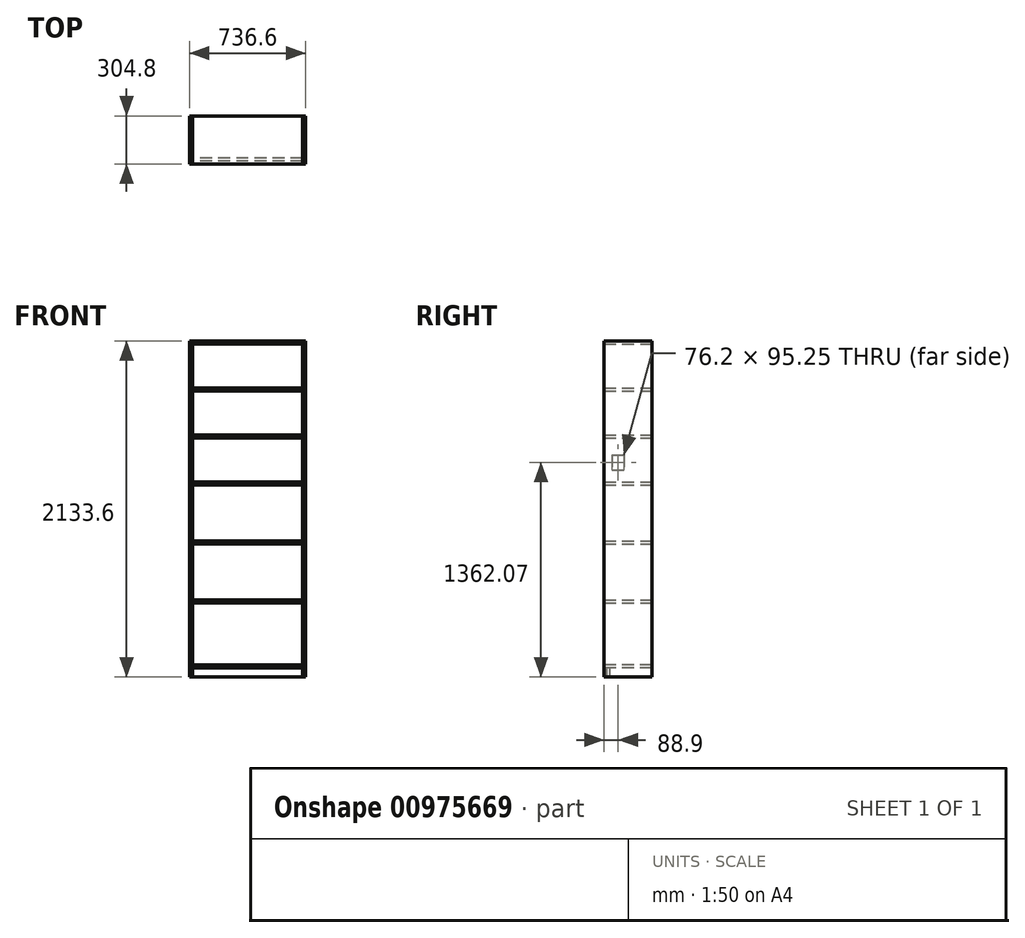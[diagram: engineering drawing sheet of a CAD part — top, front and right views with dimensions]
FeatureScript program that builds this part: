
annotation { "Feature Type Name" : "Feature", "Feature Type Description" : "" }
export const myFeature = defineFeature(function(context is Context, id is Id, definition is map)
    precondition{}
    {
        {
            var Q0;
            Q0=qCreatedBy(makeId("Front.planeOp"),FACE);
            var sketch = newSketch(context, id + "F0", { "sketchPlane" : qUnion([Q0])});
            skLineSegment(sketch, "E0.bottom", {"start": v(-919.36, 1051.17) * mm, "end": v(-900.3, 1051.17) * mm});
            skLineSegment(sketch, "E0.top", {"start": v(-919.36, -1082.43) * mm, "end": v(-900.3, -1082.43) * mm});
            skLineSegment(sketch, "E0.left", {"start": v(-919.36, 1051.17) * mm, "end": v(-919.36, -1082.43) * mm});
            skLineSegment(sketch, "E0.right", {"start": v(-900.3, 1051.17) * mm, "end": v(-900.3, -1082.43) * mm});
            skLineSegment(sketch, "E1.bottom", {"start": v(-201.8, 1051.17) * mm, "end": v(-182.76, 1051.17) * mm});
            skLineSegment(sketch, "E1.top", {"start": v(-201.8, -1082.43) * mm, "end": v(-182.76, -1082.43) * mm});
            skLineSegment(sketch, "E1.left", {"start": v(-201.8, 1051.17) * mm, "end": v(-201.8, -1082.43) * mm});
            skLineSegment(sketch, "E1.right", {"start": v(-182.76, 1051.17) * mm, "end": v(-182.76, -1082.43) * mm});
            skSolve(sketch);
        }
        {
            var Q0;
            Q0 = qSketchRegion(id + "F0", true);
            extrude(context, id + "F1", {"entities" : qUnion([Q0]), "depth" : 304.8 * mm, "offsetDistance" : 25.4 * mm});
        }
        {
            var Q0;
            Q0=qCreatedBy(makeId("Front.planeOp"),FACE);
            var sketch = newSketch(context, id + "F2", { "sketchPlane" : qUnion([Q0])});
            skLineSegment(sketch, "E2.bottom", {"start": v(-900.3, -593.48) * mm, "end": v(-201.8, -593.48) * mm});
            skLineSegment(sketch, "E2.top", {"start": v(-900.3, -612.53) * mm, "end": v(-201.8, -612.53) * mm});
            skLineSegment(sketch, "E2.left", {"start": v(-900.3, -593.48) * mm, "end": v(-900.3, -612.53) * mm});
            skLineSegment(sketch, "E2.right", {"start": v(-201.8, -593.48) * mm, "end": v(-201.8, -612.53) * mm});
            skLineSegment(sketch, "E3.bottom", {"start": v(-900.3, -218.83) * mm, "end": v(-201.8, -218.83) * mm});
            skLineSegment(sketch, "E3.top", {"start": v(-900.3, -237.88) * mm, "end": v(-201.8, -237.88) * mm});
            skLineSegment(sketch, "E3.left", {"start": v(-900.3, -218.83) * mm, "end": v(-900.3, -237.88) * mm});
            skLineSegment(sketch, "E3.right", {"start": v(-201.8, -218.83) * mm, "end": v(-201.8, -237.88) * mm});
            skLineSegment(sketch, "E4.bottom", {"start": v(-900.3, 155.82) * mm, "end": v(-201.8, 155.82) * mm});
            skLineSegment(sketch, "E4.top", {"start": v(-900.3, 136.77) * mm, "end": v(-201.8, 136.77) * mm});
            skLineSegment(sketch, "E4.left", {"start": v(-900.3, 155.82) * mm, "end": v(-900.3, 136.77) * mm});
            skLineSegment(sketch, "E4.right", {"start": v(-201.8, 155.82) * mm, "end": v(-201.8, 136.77) * mm});
            skLineSegment(sketch, "E5.bottom", {"start": v(-900.3, 454.27) * mm, "end": v(-201.8, 454.27) * mm});
            skLineSegment(sketch, "E5.top", {"start": v(-900.3, 435.22) * mm, "end": v(-201.8, 435.22) * mm});
            skLineSegment(sketch, "E5.left", {"start": v(-900.3, 454.27) * mm, "end": v(-900.3, 435.22) * mm});
            skLineSegment(sketch, "E5.right", {"start": v(-201.8, 454.27) * mm, "end": v(-201.8, 435.22) * mm});
            skLineSegment(sketch, "E6.bottom", {"start": v(-900.3, 752.72) * mm, "end": v(-201.8, 752.72) * mm});
            skLineSegment(sketch, "E6.top", {"start": v(-900.3, 733.67) * mm, "end": v(-201.8, 733.67) * mm});
            skLineSegment(sketch, "E6.left", {"start": v(-900.3, 752.72) * mm, "end": v(-900.3, 733.67) * mm});
            skLineSegment(sketch, "E6.right", {"start": v(-201.8, 752.72) * mm, "end": v(-201.8, 733.67) * mm});
            skLineSegment(sketch, "E7.bottom", {"start": v(-900.3, 1051.17) * mm, "end": v(-201.8, 1051.17) * mm});
            skLineSegment(sketch, "E7.top", {"start": v(-900.3, 1032.12) * mm, "end": v(-201.8, 1032.12) * mm});
            skLineSegment(sketch, "E7.left", {"start": v(-900.3, 1051.17) * mm, "end": v(-900.3, 1032.12) * mm});
            skLineSegment(sketch, "E7.right", {"start": v(-201.8, 1051.17) * mm, "end": v(-201.8, 1032.12) * mm});
            skSolve(sketch);
        }
        {
            var Q0;
            Q0 = qSketchRegion(id + "F2", true);
            extrude(context, id + "F3", {"entities" : qUnion([Q0]), "depth" : 304.8 * mm, "offsetDistance" : 25.4 * mm});
        }
        {
            var Q0;
            Q0=makeQuery(id+"F3.opExtrude","CAP_FACE",FACE,{"disambiguationData":[OSD([sQuery(id+"F2.wireOp",EDGE,"E2.bottom"),sQuery(id+"F2.wireOp",EDGE,"E2.top"),sQuery(id+"F2.wireOp",EDGE,"E2.left"),sQuery(id+"F2.wireOp",EDGE,"E2.right")])],"isStart":false});
            var sketch = newSketch(context, id + "F4", { "sketchPlane" : qUnion([Q0])});
            skLineSegment(sketch, "E8.bottom", {"start": v(-900.3, -1006.23) * mm, "end": v(-201.8, -1006.23) * mm});
            skLineSegment(sketch, "E8.top", {"start": v(-900.3, -1025.28) * mm, "end": v(-201.8, -1025.28) * mm});
            skLineSegment(sketch, "E8.left", {"start": v(-900.3, -1006.23) * mm, "end": v(-900.3, -1025.28) * mm});
            skLineSegment(sketch, "E8.right", {"start": v(-201.8, -1006.23) * mm, "end": v(-201.8, -1025.28) * mm});
            skSolve(sketch);
        }
        {
            var Q0;
            Q0 = qSketchRegion(id + "F4", true);
            extrude(context, id + "F5", {"entities" : qUnion([Q0]), "oppositeDirection" : true, "depth" : 304.8 * mm, "offsetDistance" : 25.4 * mm});
        }
        {
            var Q0;
            Q0=makeQuery(id+"F5.opExtrude","SWEPT_FACE",FACE,{"disambiguationData":[OSD([sQuery(id+"F4.wireOp",EDGE,"E8.top")])]});
            var sketch = newSketch(context, id + "F6", { "sketchPlane" : qUnion([Q0])});
            skLineSegment(sketch, "E9.bottom", {"start": v(-900.3, 285.75) * mm, "end": v(-201.8, 285.75) * mm});
            skLineSegment(sketch, "E9.top", {"start": v(-900.3, 266.7) * mm, "end": v(-201.8, 266.7) * mm});
            skLineSegment(sketch, "E9.left", {"start": v(-900.3, 285.75) * mm, "end": v(-900.3, 266.7) * mm});
            skLineSegment(sketch, "E9.right", {"start": v(-201.8, 285.75) * mm, "end": v(-201.8, 266.7) * mm});
            skSolve(sketch);
        }
        {
            var Q0;
            Q0 = qSketchRegion(id + "F6", true);
            var Q1;
            Q1=makeQuery(id+"F1.opExtrude","SWEPT_FACE",FACE,{"disambiguationData":[OSD([sQuery(id+"F0.wireOp",EDGE,"E0.top")])]});
            extrude(context, id + "F7", {"entities" : qUnion([Q0]), "endBound" : BoundingType.UP_TO_SURFACE, "depth" : 25.4 * mm, "endBoundEntityFace" : qUnion([Q1]), "offsetDistance" : 25.4 * mm});
        }
        {
            var Q0;
            Q0=makeQuery(id+"F1.opExtrude","SWEPT_FACE",FACE,{"disambiguationData":[OSD([sQuery(id+"F0.wireOp",EDGE,"E0.right")])]});
            var sketch = newSketch(context, id + "F8", { "sketchPlane" : qUnion([Q0])});
            skLineSegment(sketch, "E10.bottom", {"start": v(-254, 327.27) * mm, "end": v(-177.8, 327.27) * mm});
            skLineSegment(sketch, "E10.top", {"start": v(-254, 232.02) * mm, "end": v(-177.8, 232.02) * mm});
            skLineSegment(sketch, "E10.left", {"start": v(-254, 327.27) * mm, "end": v(-254, 232.02) * mm});
            skLineSegment(sketch, "E10.right", {"start": v(-177.8, 327.27) * mm, "end": v(-177.8, 232.02) * mm});
            skSolve(sketch);
        }
        {
            var Q0;
            Q0 = qSketchRegion(id + "F8", true);
            extrude(context, id + "F9", {"entities" : qUnion([Q0]), "operationType" : NewBodyOperationType.REMOVE, "oppositeDirection" : true, "depth" : 25.4 * mm, "offsetDistance" : 25.4 * mm});
        }
    });
